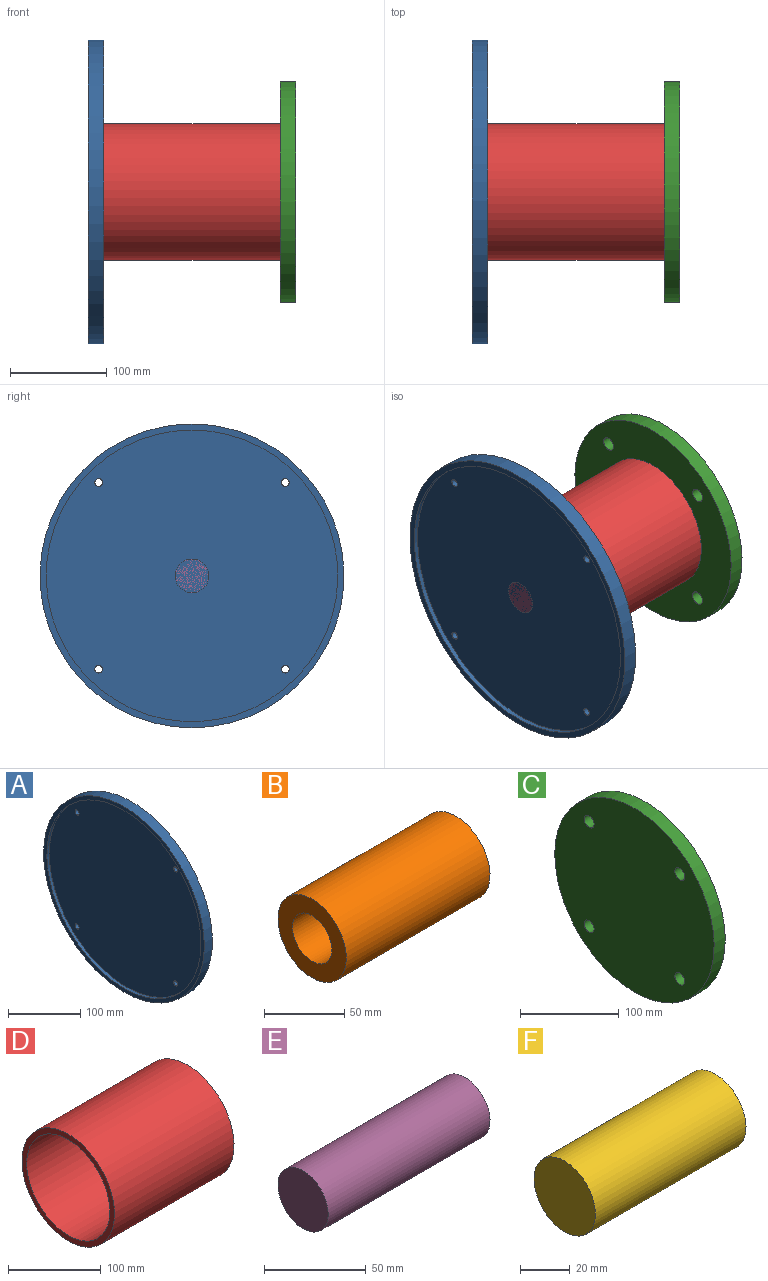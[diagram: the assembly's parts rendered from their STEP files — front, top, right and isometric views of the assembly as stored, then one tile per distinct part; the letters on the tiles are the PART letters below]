
ASSEMBLY  parts=6 mates=6
PART A: 9 faces, bbox 15.9x314.3x314.3 mm
  f0: cylinder r=157.16mm len=314.33mm, axis (-1,0,0), area 15676.3mm2, adj f1,f2
  f1: plane 314.33x314.33mm, normal (1,0,0), area 77399.6mm2, adj f0,f5,f6,f7,f8
  f2: plane 314.33x314.33mm, normal (-1,0,0), area 6143.8mm2, adj f0,f3
  f3: cylinder r=150.81mm len=301.63mm, axis (-1,0,0), area 4512.9mm2, adj f2,f4
  f4: plane 301.63x301.63mm, normal (-1,0,0), area 71255.7mm2, adj f3,f5,f6,f7,f8
  f5: cylinder r=3.97mm len=11.11mm, axis (-1,0,0), area 277.1mm2, adj f1,f4
  f6: cylinder r=3.97mm len=11.11mm, axis (-1,0,0), area 277.1mm2, adj f1,f4
  f7: cylinder r=3.97mm len=11.11mm, axis (-1,0,0), area 277.1mm2, adj f1,f4
  f8: cylinder r=3.97mm len=11.11mm, axis (-1,0,0), area 277.1mm2, adj f1,f4
PART B: 4 faces, bbox 127x60.3x60.3 mm
  f0: cylinder r=17.46mm len=127mm, axis (-1,0,0), area 13934.5mm2, adj f2,f3
  f1: cylinder r=30.16mm len=127mm, axis (-1,0,0), area 24068.6mm2, adj f2,f3
  f2: plane 60.33x60.33mm, normal (1,0,0), area 1900.2mm2, adj f0,f1
  f3: plane 60.33x60.33mm, normal (-1,0,0), area 1900.2mm2, adj f0,f1
PART C: 9 faces, bbox 15.9x228.6x228.6 mm
  f0: cylinder r=114.3mm len=228.6mm, axis (-1,0,0), area 11400.9mm2, adj f1,f2
  f1: plane 228.6x228.6mm, normal (1,0,0), area 4433.7mm2, adj f0,f3
  f2: plane 228.6x228.6mm, normal (-1,0,0), area 40402mm2, adj f0,f5,f6,f7,f8
  f3: cylinder r=107.95mm len=215.9mm, axis (1,0,0), area 3230.3mm2, adj f1,f4
  f4: plane 215.9x215.9mm, normal (1,0,0), area 35968.3mm2, adj f3,f5,f6,f7,f8
  f5: cylinder r=7.14mm len=14.29mm, axis (1,0,0), area 498.8mm2, adj f2,f4
  f6: cylinder r=7.14mm len=14.29mm, axis (1,0,0), area 498.8mm2, adj f2,f4
  f7: cylinder r=7.14mm len=14.29mm, axis (1,0,0), area 498.8mm2, adj f2,f4
  f8: cylinder r=7.14mm len=14.29mm, axis (1,0,0), area 498.8mm2, adj f2,f4
PART D: 4 faces, bbox 182.6x141.3x141.3 mm
  f0: cylinder r=63.5mm len=182.56mm, axis (-1,0,0), area 72839.2mm2, adj f2,f3
  f1: cylinder r=70.64mm len=182.56mm, axis (-1,0,0), area 81033.6mm2, adj f2,f3
  f2: plane 141.29x141.29mm, normal (1,0,0), area 3010.6mm2, adj f0,f1
  f3: plane 141.29x141.29mm, normal (-1,0,0), area 3010.6mm2, adj f0,f1
PART E: 3 faces, bbox 112.7x34.9x34.9 mm
  f0: cylinder r=17.46mm len=112.71mm, axis (-1,0,0), area 12366.8mm2, adj f1,f2
  f1: plane 34.93x34.93mm, normal (1,0,0), area 958mm2, adj f0
  f2: plane 34.93x34.93mm, normal (-1,0,0), area 958mm2, adj f0
PART F: 3 faces, bbox 85.7x34.9x34.9 mm
  f0: cylinder r=17.46mm len=85.73mm, axis (-1,0,0), area 9405.8mm2, adj f1,f2
  f1: plane 34.93x34.93mm, normal (1,0,0), area 958mm2, adj f0
  f2: plane 34.93x34.93mm, normal (-1,0,0), area 958mm2, adj f0
PLACE A t=(-209.55,0,0)mm
PLACE B t=(-152.4,0,0)mm
PLACE C t=(-11.11,0,0)mm
PLACE D t=(-193.68,0,0)mm
PLACE E t=(-204.79,0,0)mm
PLACE F t=(-85.72,0,0)mm
MATE fastened D.f1 <-> A.f0  axis (-1,0,0) through (-193.68,0,0)mm
MATE slider A.f0 <-> C.f0  axis (1,0,0) through (-193.68,0,0)mm
MATE fastened E.f0 <-> F.f0  axis (1,0,0) through (-92.08,0,0)mm
MATE fastened A.f3 <-> E.f0  axis (-1,0,0) through (-204.79,0,0)mm
MATE fastened B.f0 <-> F.f0  axis (1,0,0) through (-25.4,0,0)mm
MATE fastened C.f3 <-> F.f0  axis (1,0,0) through (0,0,0)mm
